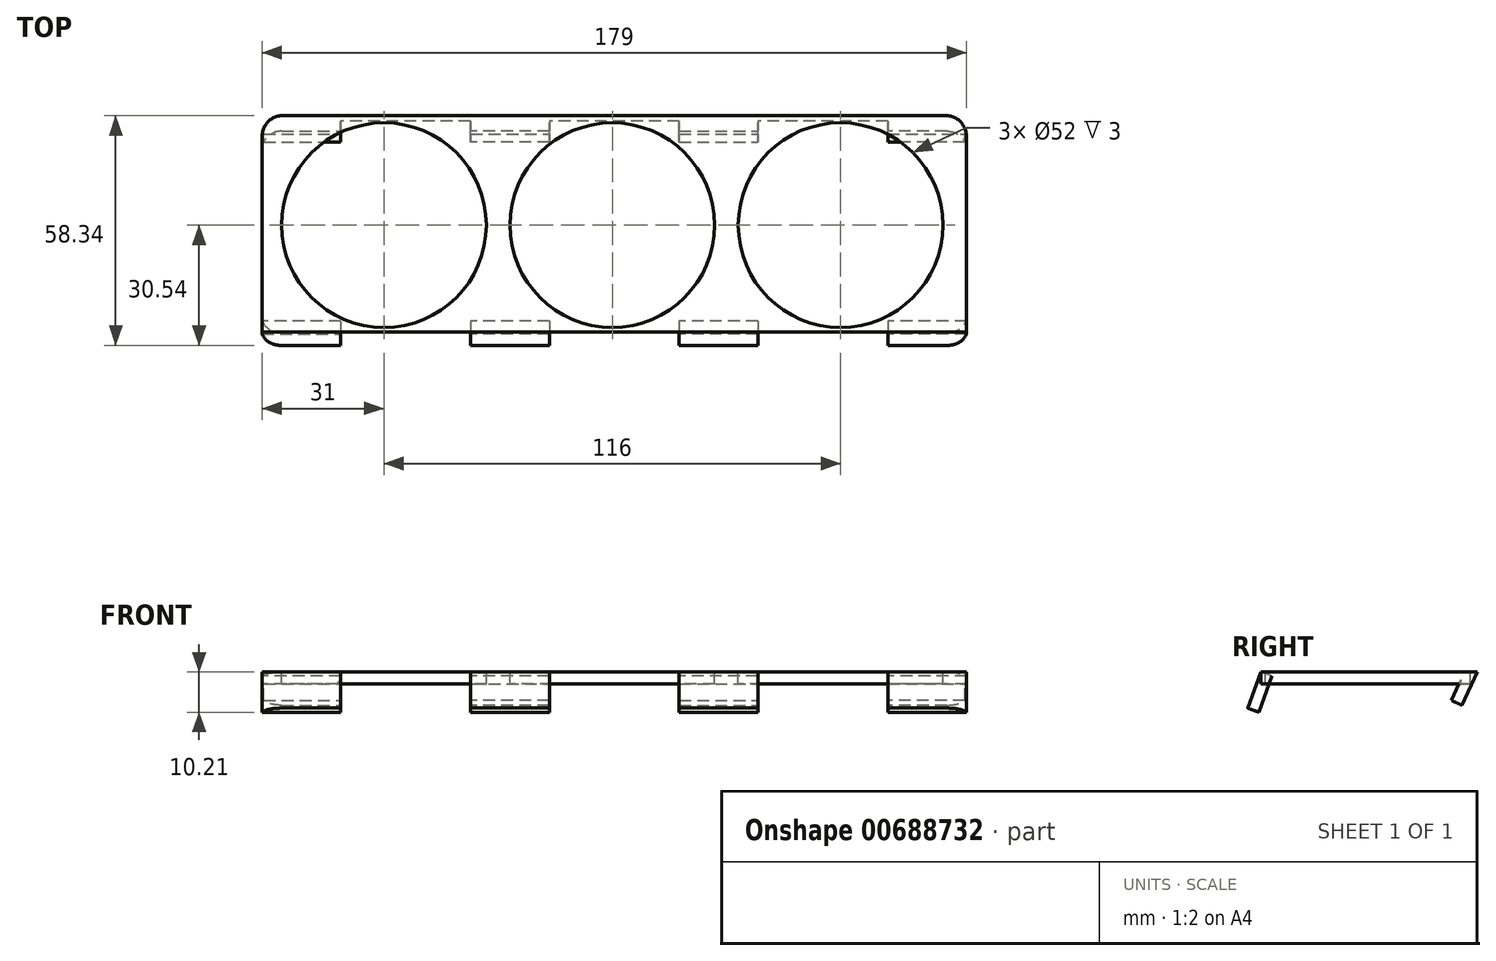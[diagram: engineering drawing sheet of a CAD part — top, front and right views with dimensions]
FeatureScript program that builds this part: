
annotation { "Feature Type Name" : "Feature", "Feature Type Description" : "" }
export const myFeature = defineFeature(function(context is Context, id is Id, definition is map)
    precondition{}
    {
        {
            var Q0;
            Q0=qCreatedBy(makeId("Top.planeOp"),FACE);
            var sketch = newSketch(context, id + "F0", { "sketchPlane" : qUnion([Q0])});
            skLineSegment(sketch, "E0.bottom", {"start": v(0, 0) * mm, "end": v(-179, 0) * mm});
            skLineSegment(sketch, "E0.top", {"start": v(0, 55) * mm, "end": v(-179, 55) * mm});
            skLineSegment(sketch, "E0.left", {"start": v(0, 0) * mm, "end": v(0, 55) * mm});
            skLineSegment(sketch, "E0.right", {"start": v(-179, 0) * mm, "end": v(-179, 55) * mm});
            skCircle(sketch, "E1", {"center": v(-148, 27.2) * mm, "radius": 26 * mm});
            skCircle(sketch, "E2.1.0.0", {"center": v(-90, 27.2) * mm, "radius": 26 * mm});
            skCircle(sketch, "E2.2.0.0", {"center": v(-32, 27.2) * mm, "radius": 26 * mm});
            skLineSegment(sketch, "E2.direction1", {"start": v(-148, 27.2) * mm, "end": v(-90, 27.2) * mm, "construction": true});
            skSolve(sketch);
        }
        {
            var Q0;
            Q0=makeQuery(id+"F0.imprint","IMPRINT",FACE,{"disambiguationData":[TD([[makeQuery(id+"F0.imprint","IMPRINT",EDGE,{"derivedFrom":sQuery(id+"F0.wireOp",EDGE,"E0.bottom")}),-1.0]])]});
            extrude(context, id + "F1", {"entities" : qUnion([Q0]), "oppositeDirection" : true, "depth" : 3 * mm, "offsetDistance" : 25 * mm});
        }
        {
            var Q0;
            Q0=makeQuery(id+"F1.opExtrude","CAP_EDGE",EDGE,{"disambiguationData":[OSD([sQuery(id+"F0.wireOp",EDGE,"E0.top")])],"isStart":true});
            cPlane(context, id + "F2", {"entities" : qUnion([Q0]), "cplaneType" : CPlaneType.LINE_ANGLE, "offset" : 25 * mm, "angle" : 25 * degree, "width" : 150 * mm, "height" : 150 * mm});
        }
        {
            var Q0;
            Q0=makeQuery(id+"F1.opExtrude","CAP_EDGE",EDGE,{"disambiguationData":[OSD([sQuery(id+"F0.wireOp",EDGE,"E0.bottom")])],"isStart":true});
            cPlane(context, id + "F3", {"entities" : qUnion([Q0]), "cplaneType" : CPlaneType.LINE_ANGLE, "offset" : 25 * mm, "angle" : 20 * degree, "width" : 150 * mm, "height" : 150 * mm});
        }
        {
            var Q0;
            Q0=qCreatedBy(id+"F2.planeOp",FACE);
            var sketch = newSketch(context, id + "F4", { "sketchPlane" : qUnion([Q0])});
            skLineSegment(sketch, "E3.0", {"start": v(0, 23.24) * mm, "end": v(-179, 23.24) * mm});
            skLineSegment(sketch, "E4.bottom", {"start": v(-179, 23.24) * mm, "end": v(0, 23.24) * mm});
            skLineSegment(sketch, "E4.top", {"start": v(-179, 11.18) * mm, "end": v(0, 11.18) * mm});
            skLineSegment(sketch, "E4.left", {"start": v(-179, 23.24) * mm, "end": v(-179, 11.18) * mm});
            skLineSegment(sketch, "E4.right", {"start": v(0, 23.24) * mm, "end": v(0, 11.18) * mm});
            skSolve(sketch);
        }
        {
            var Q0;
            Q0=makeQuery(id+"F1.opExtrude","SWEPT_FACE",FACE,{"disambiguationData":[OSD([sQuery(id+"F0.wireOp",EDGE,"E0.right")])]});
            cPlane(context, id + "F5", {"entities" : qUnion([Q0]), "cplaneType" : CPlaneType.OFFSET, "offset" : 0 * mm, "width" : 150 * mm, "height" : 150 * mm});
        }
        {
            var Q0;
            Q0=qCreatedBy(id+"F5.planeOp",FACE);
            var sketch = newSketch(context, id + "F6", { "sketchPlane" : qUnion([Q0])});
            skLineSegment(sketch, "E5.0", {"start": v(-55, 0) * mm, "end": v(-49.9, -10.93) * mm});
            skLineSegment(sketch, "E6", {"start": v(-55, 0) * mm, "end": v(-57.27, -1.06) * mm});
            skLineSegment(sketch, "E7", {"start": v(-57.27, -1.06) * mm, "end": v(-52.25, -11.84) * mm});
            skLineSegment(sketch, "E8", {"start": v(-52.25, -11.84) * mm, "end": v(-49.9, -10.93) * mm});
            skSolve(sketch);
        }
        {
            var Q0;
            Q0=makeQuery(id+"F6.imprint","IMPRINT",FACE,{"disambiguationData":[TD([[makeQuery(id+"F6.imprint","IMPRINT",EDGE,{"derivedFrom":sQuery(id+"F6.wireOp",EDGE,"E5.0")}),-1.0]])]});
            extrude(context, id + "F7", {"entities" : qUnion([Q0]), "operationType" : NewBodyOperationType.REMOVE, "endBound" : BoundingType.THROUGH_ALL, "oppositeDirection" : true, "depth" : 25 * mm, "offsetDistance" : 25 * mm});
        }
        {
            var Q0;
            Q0=qCreatedBy(id+"F2.planeOp",FACE);
            var sketch = newSketch(context, id + "F8", { "sketchPlane" : qUnion([Q0])});
            skLineSegment(sketch, "E9.0", {"start": v(0, 19.93) * mm, "end": v(-179, 19.93) * mm});
            skLineSegment(sketch, "E10.bottom", {"start": v(0, 19.93) * mm, "end": v(-20, 19.93) * mm});
            skLineSegment(sketch, "E10.top", {"start": v(0, 13.93) * mm, "end": v(-20, 13.93) * mm});
            skLineSegment(sketch, "E10.left", {"start": v(0, 19.93) * mm, "end": v(0, 13.93) * mm});
            skLineSegment(sketch, "E10.right", {"start": v(-20, 19.93) * mm, "end": v(-20, 13.93) * mm});
            skLineSegment(sketch, "E11.bottom", {"start": v(-179, 19.93) * mm, "end": v(-159, 19.93) * mm});
            skLineSegment(sketch, "E11.top", {"start": v(-179, 13.93) * mm, "end": v(-159, 13.93) * mm});
            skLineSegment(sketch, "E11.left", {"start": v(-179, 19.93) * mm, "end": v(-179, 13.93) * mm});
            skLineSegment(sketch, "E11.right", {"start": v(-159, 19.93) * mm, "end": v(-159, 13.93) * mm});
            skLineSegment(sketch, "E12.bottom", {"start": v(-106, 19.93) * mm, "end": v(-126, 19.93) * mm});
            skLineSegment(sketch, "E12.top", {"start": v(-106, 13.93) * mm, "end": v(-126, 13.93) * mm});
            skLineSegment(sketch, "E12.left", {"start": v(-106, 19.93) * mm, "end": v(-106, 13.93) * mm});
            skLineSegment(sketch, "E12.right", {"start": v(-126, 19.93) * mm, "end": v(-126, 13.93) * mm});
            skLineSegment(sketch, "E13.bottom", {"start": v(-73, 19.93) * mm, "end": v(-53, 19.93) * mm});
            skLineSegment(sketch, "E13.top", {"start": v(-73, 13.93) * mm, "end": v(-53, 13.93) * mm});
            skLineSegment(sketch, "E13.left", {"start": v(-73, 19.93) * mm, "end": v(-73, 13.93) * mm});
            skLineSegment(sketch, "E13.right", {"start": v(-53, 19.93) * mm, "end": v(-53, 13.93) * mm});
            skSolve(sketch);
        }
        {
            var Q0;
            Q0 = qSketchRegion(id + "F8", true);
            extrude(context, id + "F9", {"entities" : qUnion([Q0]), "operationType" : NewBodyOperationType.ADD, "depth" : 3 * mm, "offsetDistance" : 25 * mm});
        }
        {
            var Q0;
            Q0=qCreatedBy(id+"F3.planeOp",FACE);
            var sketch = newSketch(context, id + "F10", { "sketchPlane" : qUnion([Q0])});
            skLineSegment(sketch, "E14.0", {"start": v(0, 0) * mm, "end": v(-179, 0) * mm});
            skLineSegment(sketch, "E15.bottom", {"start": v(0, 0) * mm, "end": v(-20, 0) * mm});
            skLineSegment(sketch, "E15.top", {"start": v(0, -9.77) * mm, "end": v(-20, -9.77) * mm});
            skLineSegment(sketch, "E15.left", {"start": v(0, 0) * mm, "end": v(0, -9.77) * mm});
            skLineSegment(sketch, "E15.right", {"start": v(-20, 0) * mm, "end": v(-20, -9.77) * mm});
            skLineSegment(sketch, "E16.bottom", {"start": v(-179, 0) * mm, "end": v(-159, 0) * mm});
            skLineSegment(sketch, "E16.top", {"start": v(-179, -9.77) * mm, "end": v(-159, -9.77) * mm});
            skLineSegment(sketch, "E16.left", {"start": v(-179, 0) * mm, "end": v(-179, -9.77) * mm});
            skLineSegment(sketch, "E16.right", {"start": v(-159, 0) * mm, "end": v(-159, -9.77) * mm});
            skLineSegment(sketch, "E17.bottom", {"start": v(-53, 0) * mm, "end": v(-73, 0) * mm});
            skLineSegment(sketch, "E17.top", {"start": v(-53, -9.77) * mm, "end": v(-73, -9.77) * mm});
            skLineSegment(sketch, "E17.left", {"start": v(-53, 0) * mm, "end": v(-53, -9.77) * mm});
            skLineSegment(sketch, "E17.right", {"start": v(-73, 0) * mm, "end": v(-73, -9.77) * mm});
            skLineSegment(sketch, "E18.bottom", {"start": v(-106, 0) * mm, "end": v(-126, 0) * mm});
            skLineSegment(sketch, "E18.top", {"start": v(-106, -9.77) * mm, "end": v(-126, -9.77) * mm});
            skLineSegment(sketch, "E18.left", {"start": v(-106, 0) * mm, "end": v(-106, -9.77) * mm});
            skLineSegment(sketch, "E18.right", {"start": v(-126, 0) * mm, "end": v(-126, -9.77) * mm});
            skSolve(sketch);
        }
        {
            var Q0;
            Q0 = qSketchRegion(id + "F10", true);
            extrude(context, id + "F11", {"entities" : qUnion([Q0]), "oppositeDirection" : true, "depth" : 3 * mm, "offsetDistance" : 25 * mm});
        }
        {
            var Q0;
            Q0=makeQuery(id+"F9.boolean.opBoolean","MERGE",EDGE,{"derivedFrom":[makeQuery(id+"F7.boolean.opBoolean","INTERSECT",EDGE,{"derivedFrom":[makeQuery(id+"F1.opExtrude","SWEPT_FACE",FACE,{"disambiguationData":[OSD([sQuery(id+"F0.wireOp",EDGE,"E0.left")])]}),makeQuery(id+"F7.opExtrude","SWEPT_FACE",FACE,{"disambiguationData":[OSD([sQuery(id+"F6.wireOp",EDGE,"E5.0")])]})]}),makeQuery(id+"F9.opExtrude","CAP_EDGE",EDGE,{"disambiguationData":[OSD([sQuery(id+"F8.wireOp",EDGE,"E10.left")])],"isStart":true})]});
            var Q1;
            Q1=makeQuery(id+"F11.opExtrude","CAP_EDGE",EDGE,{"disambiguationData":[OSD([sQuery(id+"F10.wireOp",EDGE,"E15.left")])],"isStart":true});
            var Q2;
            Q2=makeQuery(id+"F11.opExtrude","CAP_EDGE",EDGE,{"disambiguationData":[OSD([sQuery(id+"F10.wireOp",EDGE,"E16.left")])],"isStart":true});
            var Q3;
            Q3=makeQuery(id+"F9.boolean.opBoolean","MERGE",EDGE,{"derivedFrom":[makeQuery(id+"F7.boolean.opBoolean","COPY",EDGE,{"derivedFrom":makeQuery(id+"F7.opExtrude","CAP_EDGE",EDGE,{"disambiguationData":[OSD([sQuery(id+"F6.wireOp",EDGE,"E5.0")])],"isStart":true})}),makeQuery(id+"F9.opExtrude","CAP_EDGE",EDGE,{"disambiguationData":[OSD([sQuery(id+"F8.wireOp",EDGE,"E11.left")])],"isStart":true})]});
            fillet(context, id + "F12", {"entities" : qUnion([Q0, Q1, Q2, Q3]), "radius" : 5 * mm, "tangentPropagation" : true, "allowEdgeOverflow" : false});
        }
    });
